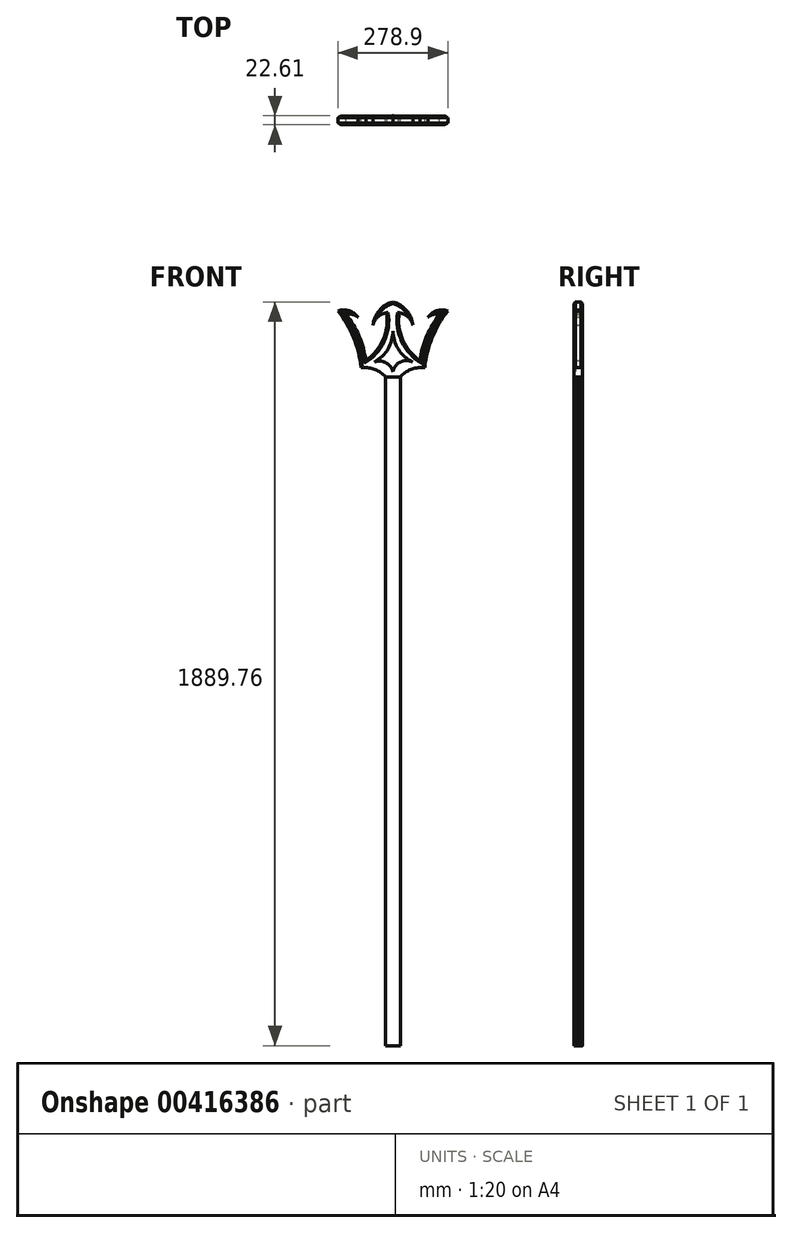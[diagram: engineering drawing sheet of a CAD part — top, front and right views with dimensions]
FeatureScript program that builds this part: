
annotation { "Feature Type Name" : "Feature", "Feature Type Description" : "" }
export const myFeature = defineFeature(function(context is Context, id is Id, definition is map)
    precondition{}
    {
        {
            var Q0;
            Q0=qCreatedBy(makeId("Top.planeOp"),FACE);
            var sketch = newSketch(context, id + "F0", { "sketchPlane" : qUnion([Q0])});
            skArc(sketch, "E0", {"start": v(-19.09, -5.01) * mm, "mid": v(-0.13, -11.3) * mm, "end": v(18.83, -5.01) * mm});
            skArc(sketch, "E1", {"start": v(18.94, 4.98) * mm, "mid": v(0.02, 11.32) * mm, "end": v(-18.95, 5.1) * mm});
            skLineSegment(sketch, "E2", {"start": v(-19.09, -5.01) * mm, "end": v(-18.95, 5.1) * mm});
            skLineSegment(sketch, "E3", {"start": v(18.83, -5.01) * mm, "end": v(18.94, 4.98) * mm});
            skSolve(sketch);
        }
        {
            var Q0;
            Q0=makeQuery(id+"F0.imprint","IMPRINT",FACE,{"disambiguationData":[TD([[makeQuery(id+"F0.imprint","IMPRINT",EDGE,{"derivedFrom":sQuery(id+"F0.wireOp",EDGE,"E0")}),1.0]])]});
            extrude(context, id + "F1", {"entities" : qUnion([Q0]), "oppositeDirection" : true, "depth" : 1699.26 * mm});
        }
        {
            var Q0;
            Q0=qCreatedBy(makeId("Front.planeOp"),FACE);
            var sketch = newSketch(context, id + "F2", { "sketchPlane" : qUnion([Q0])});
            skLineSegment(sketch, "E4", {"start": v(0, 0) * mm, "end": v(0, 190.5) * mm});
            skArc(sketch, "E5", {"start": v(139.45, 167.53) * mm, "mid": v(99.94, 99.87) * mm, "end": v(80.96, 23.84) * mm});
            skArc(sketch, "E6", {"start": v(139.45, 167.53) * mm, "mid": v(111.64, 167.94) * mm, "end": v(89.02, 151.73) * mm});
            skArc(sketch, "E7", {"start": v(50.6, 131.1) * mm, "mid": v(34.57, 168.7) * mm, "end": v(0, 190.5) * mm});
            skArc(sketch, "E8", {"start": v(50.6, 131.1) * mm, "mid": v(38.42, 152.3) * mm, "end": v(16.28, 162.67) * mm});
            skArc(sketch, "E9", {"start": v(16.28, 162.67) * mm, "mid": v(24.7, 94.38) * mm, "end": v(68.88, 41.63) * mm});
            skArc(sketch, "E10", {"start": v(118.89, 158.47) * mm, "mid": v(103.16, 158.62) * mm, "end": v(89.02, 151.73) * mm});
            skArc(sketch, "E11", {"start": v(118.89, 158.47) * mm, "mid": v(85.84, 103.5) * mm, "end": v(68.88, 41.63) * mm});
            skLineSegment(sketch, "E12", {"start": v(0, 0) * mm, "end": v(18.77, 0) * mm});
            skArc(sketch, "E13", {"start": v(80.96, 23.84) * mm, "mid": v(47.12, 19.08) * mm, "end": v(18.77, 0) * mm});
            skSolve(sketch);
        }
        {
            var Q0;
            Q0=makeQuery(id+"F2.imprint","IMPRINT",FACE,{"disambiguationData":[TD([[makeQuery(id+"F2.imprint","IMPRINT",EDGE,{"derivedFrom":sQuery(id+"F2.wireOp",EDGE,"E4")}),-1.0]])]});
            extrude(context, id + "F3", {"entities" : qUnion([Q0]), "depth" : 10.8 * mm, "hasSecondDirection" : true, "secondDirectionOppositeDirection" : true, "secondDirectionDepth" : 10.8 * mm});
        }
        {
            var Q0;
            Q0=makeQuery(id+"F3.opExtrude","SWEPT_BODY",BODY,{"disambiguationData":[OSD([sQuery(id+"F2.wireOp",EDGE,"E4"),sQuery(id+"F2.wireOp",EDGE,"i21JQWpV-gtiF-KeSc-gDDn-s9V6elZGldy9"),sQuery(id+"F2.wireOp",EDGE,"E5"),sQuery(id+"F2.wireOp",EDGE,"E6"),sQuery(id+"F2.wireOp",EDGE,"E7"),sQuery(id+"F2.wireOp",EDGE,"E8"),sQuery(id+"F2.wireOp",EDGE,"E9"),sQuery(id+"F2.wireOp",EDGE,"E10"),sQuery(id+"F2.wireOp",EDGE,"E11")])]});
            var Q1;
            Q1=qCreatedBy(makeId("Right.planeOp"),FACE);
            mirror(context, id + "F4", {"operationType" : NewBodyOperationType.ADD, "entities" : qUnion([Q0]), "mirrorPlane" : qUnion([Q1])});
        }
        {
            var Q0;
            Q0=makeQuery(id+"F3.opExtrude","CAP_EDGE",EDGE,{"disambiguationData":[OSD([sQuery(id+"F2.wireOp",EDGE,"E7")])],"isStart":false});
            var Q1;
            Q1=makeQuery(id+"F4.opPattern","COPY",EDGE,{"derivedFrom":makeQuery(id+"F3.opExtrude","CAP_EDGE",EDGE,{"disambiguationData":[OSD([sQuery(id+"F2.wireOp",EDGE,"E7")])],"isStart":false}),"instanceName":"1"});
            var Q2;
            Q2=makeQuery(id+"F4.opPattern","COPY",EDGE,{"derivedFrom":makeQuery(id+"F3.opExtrude","CAP_EDGE",EDGE,{"disambiguationData":[OSD([sQuery(id+"F2.wireOp",EDGE,"E7")])],"isStart":true}),"instanceName":"1"});
            var Q3;
            Q3=makeQuery(id+"F3.opExtrude","CAP_EDGE",EDGE,{"disambiguationData":[OSD([sQuery(id+"F2.wireOp",EDGE,"E7")])],"isStart":true});
            var Q4;
            Q4=makeQuery(id+"F3.opExtrude","CAP_EDGE",EDGE,{"disambiguationData":[OSD([sQuery(id+"F2.wireOp",EDGE,"E6")])],"isStart":false});
            var Q5;
            Q5=makeQuery(id+"F3.opExtrude","CAP_EDGE",EDGE,{"disambiguationData":[OSD([sQuery(id+"F2.wireOp",EDGE,"E6")])],"isStart":true});
            var Q6;
            Q6=makeQuery(id+"F4.opPattern","COPY",EDGE,{"derivedFrom":makeQuery(id+"F3.opExtrude","CAP_EDGE",EDGE,{"disambiguationData":[OSD([sQuery(id+"F2.wireOp",EDGE,"E6")])],"isStart":false}),"instanceName":"1"});
            var Q7;
            Q7=makeQuery(id+"F4.opPattern","COPY",EDGE,{"derivedFrom":makeQuery(id+"F3.opExtrude","CAP_EDGE",EDGE,{"disambiguationData":[OSD([sQuery(id+"F2.wireOp",EDGE,"E6")])],"isStart":true}),"instanceName":"1"});
            var Q8;
            Q8=makeQuery(id+"F4.opPattern","COPY",EDGE,{"derivedFrom":makeQuery(id+"F3.opExtrude","CAP_EDGE",EDGE,{"disambiguationData":[OSD([sQuery(id+"F2.wireOp",EDGE,"E5")])],"isStart":false}),"instanceName":"1"});
            var Q9;
            Q9=makeQuery(id+"F4.opPattern","COPY",EDGE,{"derivedFrom":makeQuery(id+"F3.opExtrude","CAP_EDGE",EDGE,{"disambiguationData":[OSD([sQuery(id+"F2.wireOp",EDGE,"E11")])],"isStart":false}),"instanceName":"1"});
            var Q10;
            Q10=makeQuery(id+"F4.opPattern","COPY",EDGE,{"derivedFrom":makeQuery(id+"F3.opExtrude","CAP_EDGE",EDGE,{"disambiguationData":[OSD([sQuery(id+"F2.wireOp",EDGE,"E11")])],"isStart":true}),"instanceName":"1"});
            var Q11;
            Q11=makeQuery(id+"F4.opPattern","COPY",EDGE,{"derivedFrom":makeQuery(id+"F3.opExtrude","CAP_EDGE",EDGE,{"disambiguationData":[OSD([sQuery(id+"F2.wireOp",EDGE,"E9")])],"isStart":false}),"instanceName":"1"});
            var Q12;
            Q12=makeQuery(id+"F3.opExtrude","CAP_EDGE",EDGE,{"disambiguationData":[OSD([sQuery(id+"F2.wireOp",EDGE,"E9")])],"isStart":false});
            var Q13;
            Q13=makeQuery(id+"F3.opExtrude","CAP_EDGE",EDGE,{"disambiguationData":[OSD([sQuery(id+"F2.wireOp",EDGE,"E9")])],"isStart":true});
            var Q14;
            Q14=makeQuery(id+"F3.opExtrude","CAP_EDGE",EDGE,{"disambiguationData":[OSD([sQuery(id+"F2.wireOp",EDGE,"E11")])],"isStart":false});
            var Q15;
            Q15=makeQuery(id+"F3.opExtrude","CAP_EDGE",EDGE,{"disambiguationData":[OSD([sQuery(id+"F2.wireOp",EDGE,"E5")])],"isStart":false});
            var Q16;
            Q16=makeQuery(id+"F3.opExtrude","CAP_EDGE",EDGE,{"disambiguationData":[OSD([sQuery(id+"F2.wireOp",EDGE,"E5")])],"isStart":true});
            var Q17;
            Q17=makeQuery(id+"F3.opExtrude","CAP_EDGE",EDGE,{"disambiguationData":[OSD([sQuery(id+"F2.wireOp",EDGE,"E11")])],"isStart":true});
            var Q18;
            Q18=makeQuery(id+"F4.opPattern","COPY",EDGE,{"derivedFrom":makeQuery(id+"F3.opExtrude","CAP_EDGE",EDGE,{"disambiguationData":[OSD([sQuery(id+"F2.wireOp",EDGE,"E9")])],"isStart":true}),"instanceName":"1"});
            var Q19;
            Q19=makeQuery(id+"F4.opPattern","COPY",EDGE,{"derivedFrom":makeQuery(id+"F3.opExtrude","CAP_EDGE",EDGE,{"disambiguationData":[OSD([sQuery(id+"F2.wireOp",EDGE,"E5")])],"isStart":true}),"instanceName":"1"});
            chamfer(context, id + "F5", {"entities" : qUnion([Q0, Q1, Q2, Q3, Q4, Q5, Q6, Q7, Q8, Q9, Q10, Q11, Q12, Q13, Q14, Q15, Q16, Q17, Q18, Q19]), "width" : 4.2 * mm, "tangentPropagation" : true});
        }
        {
            var Q0;
            {var subQ0=makeQuery(id+"F3.opExtrude","CAP_FACE",FACE,{"disambiguationData":[OSD([sQuery(id+"F2.wireOp",EDGE,"E4"),sQuery(id+"F2.wireOp",EDGE,"i21JQWpV-gtiF-KeSc-gDDn-s9V6elZGldy9"),sQuery(id+"F2.wireOp",EDGE,"E5"),sQuery(id+"F2.wireOp",EDGE,"E6"),sQuery(id+"F2.wireOp",EDGE,"E7"),sQuery(id+"F2.wireOp",EDGE,"E8"),sQuery(id+"F2.wireOp",EDGE,"E9"),sQuery(id+"F2.wireOp",EDGE,"E10"),sQuery(id+"F2.wireOp",EDGE,"E11")])],"isStart":false});Q0=makeQuery(id+"F4.boolean.opBoolean","MERGE",FACE,{"derivedFrom":[subQ0,makeQuery(id+"F4.opPattern","COPY",FACE,{"derivedFrom":subQ0,"instanceName":"1"})]});}
            var sketch = newSketch(context, id + "F6", { "sketchPlane" : qUnion([Q0])});
            skArc(sketch, "E14", {"start": v(0, 13.12) * mm, "mid": v(-17.64, 35.84) * mm, "end": v(-46.31, 38.12) * mm});
            skArc(sketch, "E15", {"start": v(49.63, 38.12) * mm, "mid": v(18.81, 37.53) * mm, "end": v(0, 13.12) * mm});
            skArc(sketch, "E16", {"start": v(-46.31, 38.12) * mm, "mid": v(-12.4, 70.95) * mm, "end": v(0, 116.5) * mm});
            skArc(sketch, "E17", {"start": v(0, 116.5) * mm, "mid": v(13.81, 70.34) * mm, "end": v(49.63, 38.12) * mm});
            skSolve(sketch);
        }
        {
            var Q0;
            Q0=makeQuery(id+"F6.imprint","IMPRINT",FACE,{"disambiguationData":[TD([[makeQuery(id+"F6.imprint","IMPRINT",EDGE,{"derivedFrom":sQuery(id+"F6.wireOp",EDGE,"E14")}),-1.0]])]});
            extrude(context, id + "F7", {"entities" : qUnion([Q0]), "operationType" : NewBodyOperationType.REMOVE, "oppositeDirection" : true, "depth" : 3.8 * mm});
        }
    });
